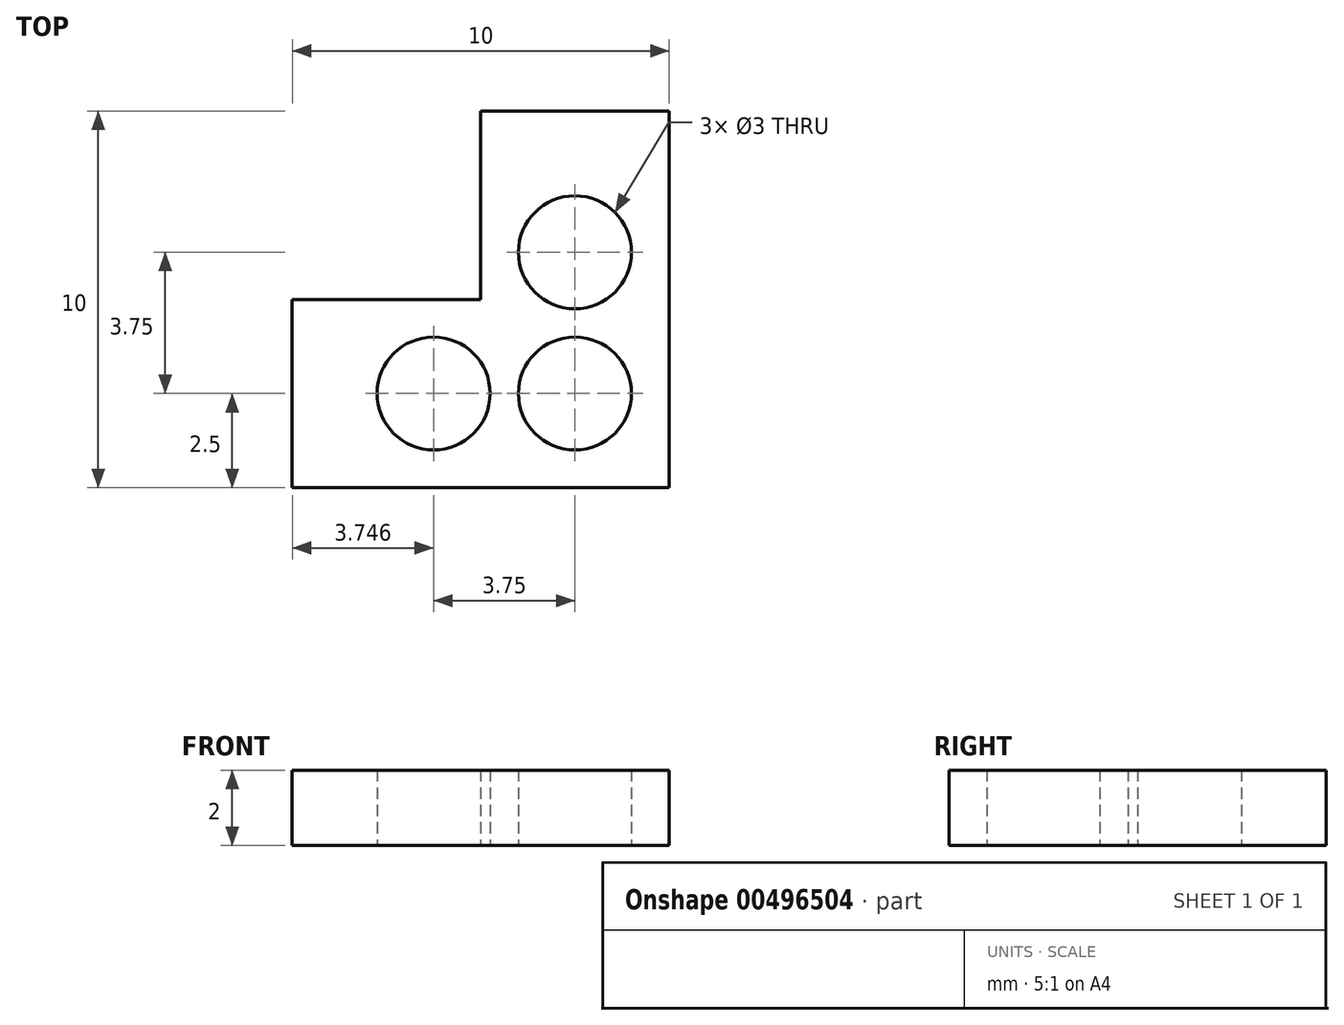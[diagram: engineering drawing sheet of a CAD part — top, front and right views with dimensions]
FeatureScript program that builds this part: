
annotation { "Feature Type Name" : "Feature", "Feature Type Description" : "" }
export const myFeature = defineFeature(function(context is Context, id is Id, definition is map)
    precondition{}
    {
        {
            var Q0;
            Q0=qCreatedBy(makeId("Top.planeOp"),FACE);
            var sketch = newSketch(context, id + "F0", { "sketchPlane" : qUnion([Q0])});
            skLineSegment(sketch, "E0.bottom", {"start": v(23.8, 16.35) * mm, "end": v(33.8, 16.35) * mm});
            skLineSegment(sketch, "E0.top", {"start": v(23.8, 21.35) * mm, "end": v(28.8, 21.35) * mm});
            skLineSegment(sketch, "E0.left", {"start": v(23.8, 16.35) * mm, "end": v(23.8, 21.35) * mm});
            skLineSegment(sketch, "E0.right", {"start": v(33.8, 16.35) * mm, "end": v(33.8, 21.35) * mm});
            skLineSegment(sketch, "E1.top", {"start": v(33.8, 26.35) * mm, "end": v(28.8, 26.35) * mm});
            skLineSegment(sketch, "E1.left", {"start": v(33.8, 21.35) * mm, "end": v(33.8, 26.35) * mm});
            skLineSegment(sketch, "E1.right", {"start": v(28.8, 21.35) * mm, "end": v(28.8, 26.35) * mm});
            skCircle(sketch, "E2", {"center": v(31.3, 22.6) * mm, "radius": 1.5 * mm});
            skCircle(sketch, "E3", {"center": v(27.55, 18.85) * mm, "radius": 1.5 * mm});
            skCircle(sketch, "E4", {"center": v(31.3, 18.85) * mm, "radius": 1.5 * mm});
            skLineSegment(sketch, "E5", {"start": v(27.55, 18.85) * mm, "end": v(23.8, 18.85) * mm, "construction": true});
            skLineSegment(sketch, "E6", {"start": v(27.55, 18.85) * mm, "end": v(31.3, 18.85) * mm, "construction": true});
            skLineSegment(sketch, "E7", {"start": v(31.3, 18.85) * mm, "end": v(31.3, 22.6) * mm, "construction": true});
            skLineSegment(sketch, "E8", {"start": v(31.3, 26.35) * mm, "end": v(31.3, 22.6) * mm, "construction": true});
            skSolve(sketch);
        }
        {
            var Q0;
            Q0=makeQuery(id+"F0.imprint","IMPRINT",FACE,{"disambiguationData":[TD([[makeQuery(id+"F0.imprint","IMPRINT",EDGE,{"derivedFrom":sQuery(id+"F0.wireOp",EDGE,"E0.bottom")}),1.0]])]});
            var Q1;
            Q1=sQuery(id+"F0.wireOp",EDGE,"E8");
            var Q2;
            Q2=sQuery(id+"F0.wireOp",EDGE,"E7");
            var Q3;
            Q3=sQuery(id+"F0.wireOp",EDGE,"E6");
            var Q4;
            Q4=sQuery(id+"F0.wireOp",EDGE,"E5");
            extrude(context, id + "F1", {"entities" : qUnion([Q0]), "surfaceEntities" : qUnion([Q1, Q2, Q3, Q4]), "depth" : 2 * mm});
        }
    });
